annotation { "Feature Type Name" : "Feature", "Feature Type Description" : "" }
export const myFeature = defineFeature(function(context is Context, id is Id, definition is map)
    precondition{}
    {
        {
            var Q0;
            Q0=qCreatedBy(makeId("Top.planeOp"),FACE);
            var sketch = newSketch(context, id + "F0", { "sketchPlane" : qUnion([Q0])});
            skLineSegment(sketch, "E0.bottom", {"start": v(-75.16, -23.95) * mm, "end": v(74.84, -23.95) * mm});
            skLineSegment(sketch, "E0.top", {"start": v(-75.16, -73.95) * mm, "end": v(74.84, -73.95) * mm});
            skLineSegment(sketch, "E0.left", {"start": v(-75.16, -23.95) * mm, "end": v(-75.16, -73.95) * mm});
            skLineSegment(sketch, "E0.right", {"start": v(74.84, -23.95) * mm, "end": v(74.84, -73.95) * mm});
            skSolve(sketch);
        }
        {
            var Q0;
            Q0=makeQuery(id+"F0.imprint","IMPRINT",FACE,{"disambiguationData":[TD([[makeQuery(id+"F0.imprint","IMPRINT",EDGE,{"derivedFrom":sQuery(id+"F0.wireOp",EDGE,"E0.bottom")}),-1.0]])]});
            extrude(context, id + "F1", {"entities" : qUnion([Q0]), "depth" : 100 * mm, "offsetDistance" : 25 * mm});
        }
        {
            var Q0;
            Q0=makeQuery(id+"F1.opExtrude","SWEPT_FACE",FACE,{"disambiguationData":[OSD([sQuery(id+"F0.wireOp",EDGE,"E0.top")])]});
            var sketch = newSketch(context, id + "F2", { "sketchPlane" : qUnion([Q0])});
            skCircle(sketch, "E1", {"center": v(26.87, 49.86) * mm, "radius": 30 * mm});
            skSolve(sketch);
        }
        {
            var Q0;
            Q0=makeQuery(id+"F2.imprint","IMPRINT",FACE,{"disambiguationData":[TD([[makeQuery(id+"F2.imprint","IMPRINT",EDGE,{"derivedFrom":sQuery(id+"F2.wireOp",EDGE,"E1")}),1.0]])]});
            extrude(context, id + "F3", {"entities" : qUnion([Q0]), "operationType" : NewBodyOperationType.ADD, "depth" : 40 * mm, "offsetDistance" : 25 * mm});
        }
        {
            var Q0;
            Q0=makeQuery(id+"F1.opExtrude","CAP_EDGE",EDGE,{"disambiguationData":[OSD([sQuery(id+"F0.wireOp",EDGE,"E0.right")])],"isStart":false});
            var Q1;
            Q1=makeQuery(id+"F1.opExtrude","CAP_EDGE",EDGE,{"disambiguationData":[OSD([sQuery(id+"F0.wireOp",EDGE,"E0.left")])],"isStart":false});
            fillet(context, id + "F4", {"entities" : qUnion([Q0, Q1]), "radius" : 5 * mm, "tangentPropagation" : true, "allowEdgeOverflow" : false});
        }
        {
            var Q0;
            Q0=makeQuery(id+"F3.opExtrude","CAP_EDGE",EDGE,{"disambiguationData":[OSD([sQuery(id+"F2.wireOp",EDGE,"E1")])],"isStart":false});
            chamfer(context, id + "F5", {"entities" : qUnion([Q0]), "width" : 5 * mm, "tangentPropagation" : true});
        }
        {
            var Q0;
            Q0=makeQuery(id+"F1.opExtrude","SWEPT_FACE",FACE,{"disambiguationData":[OSD([sQuery(id+"F0.wireOp",EDGE,"E0.top")])]});
            var sketch = newSketch(context, id + "F6", { "sketchPlane" : qUnion([Q0])});
            skText(sketch, "E2", { "text": "Nikon", "fontName": "RobotoSlab-Bold.ttf"});
            const initialGuessF6  = {"E2": [-0.07516, 0.0048, 1, 0, 0.01836]};
            skSetInitialGuess(sketch, initialGuessF6);
            skSolve(sketch);
        }
        {
            var Q0;
            Q0 = qSketchRegion(id + "F6", true);
            extrude(context, id + "F7", {"entities" : qUnion([Q0]), "operationType" : NewBodyOperationType.REMOVE, "oppositeDirection" : true, "depth" : 2 * mm, "offsetDistance" : 25 * mm});
        }
        {
            var Q0;
            {var subQ0=sQuery(id+"F0.wireOp",EDGE,"E0.left");var subQ2=sQuery(id+"F0.wireOp",EDGE,"E0.top");Q0=makeQuery(id+"F7.boolean.opBoolean","SPLIT",FACE,{"disambiguationData":[TD([makeQuery(id+"F1.opExtrude","SWEPT_FACE",FACE,{"disambiguationData":[OSD([subQ0])]})])],"derivedFrom":makeQuery(id+"F1.opExtrude","SWEPT_FACE",FACE,{"disambiguationData":[OSD([subQ2])]})});}
            var sketch = newSketch(context, id + "F8", { "sketchPlane" : qUnion([Q0])});
            skLineSegment(sketch, "E3.bottom", {"start": v(0, 97.8) * mm, "end": v(25, 97.8) * mm});
            skLineSegment(sketch, "E3.top", {"start": v(0, 87.8) * mm, "end": v(25, 87.8) * mm});
            skLineSegment(sketch, "E3.left", {"start": v(0, 97.8) * mm, "end": v(0, 87.8) * mm});
            skLineSegment(sketch, "E3.right", {"start": v(25, 97.8) * mm, "end": v(25, 87.8) * mm});
            skSolve(sketch);
        }
        {
            var Q0;
            Q0=makeQuery(id+"F8.imprint","IMPRINT",FACE,{"disambiguationData":[TD([[makeQuery(id+"F8.imprint","IMPRINT",EDGE,{"derivedFrom":sQuery(id+"F8.wireOp",EDGE,"E3.bottom")}),-1.0]])]});
            extrude(context, id + "F9", {"entities" : qUnion([Q0]), "operationType" : NewBodyOperationType.REMOVE, "oppositeDirection" : true, "depth" : 5 * mm, "offsetDistance" : 25 * mm});
        }
        {
            var Q0;
            Q0=makeQuery(id+"F1.opExtrude","CAP_FACE",FACE,{"disambiguationData":[OSD([sQuery(id+"F0.wireOp",EDGE,"E0.bottom"),sQuery(id+"F0.wireOp",EDGE,"E0.top"),sQuery(id+"F0.wireOp",EDGE,"E0.left"),sQuery(id+"F0.wireOp",EDGE,"E0.right")])],"isStart":false});
            var sketch = newSketch(context, id + "F10", { "sketchPlane" : qUnion([Q0])});
            skCircle(sketch, "E4", {"center": v(-56.66, -36) * mm, "radius": 7.42 * mm});
            skSolve(sketch);
        }
        {
            var Q0;
            Q0=makeQuery(id+"F10.imprint","IMPRINT",FACE,{"disambiguationData":[TD([[makeQuery(id+"F10.imprint","IMPRINT",EDGE,{"derivedFrom":sQuery(id+"F10.wireOp",EDGE,"E4")}),1.0]])]});
            extrude(context, id + "F11", {"entities" : qUnion([Q0]), "operationType" : NewBodyOperationType.ADD, "depth" : 5 * mm, "offsetDistance" : 25 * mm});
        }
        {
            var Q0;
            Q0=makeQuery(id+"F1.opExtrude","SWEPT_FACE",FACE,{"disambiguationData":[OSD([sQuery(id+"F0.wireOp",EDGE,"E0.bottom")])]});
            var sketch = newSketch(context, id + "F12", { "sketchPlane" : qUnion([Q0])});
            skLineSegment(sketch, "E5.bottom", {"start": v(-69.68, 79.38) * mm, "end": v(19, 79.38) * mm});
            skLineSegment(sketch, "E5.top", {"start": v(-69.68, 14) * mm, "end": v(19, 14) * mm});
            skLineSegment(sketch, "E5.left", {"start": v(-69.68, 79.38) * mm, "end": v(-69.68, 14) * mm});
            skLineSegment(sketch, "E5.right", {"start": v(19, 79.38) * mm, "end": v(19, 14) * mm});
            skSolve(sketch);
        }
        {
            var Q0;
            Q0 = qSketchRegion(id + "F12", true);
            extrude(context, id + "F13", {"entities" : qUnion([Q0]), "operationType" : NewBodyOperationType.ADD, "depth" : 1 * mm, "offsetDistance" : 25 * mm});
        }
        {
            var Q0;
            Q0=makeQuery(id+"F1.opExtrude","SWEPT_FACE",FACE,{"disambiguationData":[OSD([sQuery(id+"F0.wireOp",EDGE,"E0.bottom")])]});
            var sketch = newSketch(context, id + "F14", { "sketchPlane" : qUnion([Q0])});
            skText(sketch, "E6", { "text": "Nikon Revo", "fontName": "RobotoSlab-Bold.ttf"});
            const initialGuessF14  = {"E6": [-0.06856, 0.08341, 1, 0, 0.00806]};
            skSetInitialGuess(sketch, initialGuessF14);
            skSolve(sketch);
        }
        {
            var Q0;
            Q0 = qSketchRegion(id + "F14", true);
            extrude(context, id + "F15", {"entities" : qUnion([Q0]), "operationType" : NewBodyOperationType.REMOVE, "oppositeDirection" : true, "depth" : 2 * mm, "offsetDistance" : 25 * mm});
        }
        {
            var Q0;
            {var subQ0=sQuery(id+"F0.wireOp",EDGE,"E0.left");var subQ3=sQuery(id+"F0.wireOp",EDGE,"E0.bottom");Q0=makeQuery(id+"F15.boolean.opBoolean","SPLIT",FACE,{"disambiguationData":[TD([makeQuery(id+"F1.opExtrude","SWEPT_FACE",FACE,{"disambiguationData":[OSD([subQ0])]})])],"derivedFrom":makeQuery(id+"F1.opExtrude","SWEPT_FACE",FACE,{"disambiguationData":[OSD([subQ3])]})});}
            var sketch = newSketch(context, id + "F16", { "sketchPlane" : qUnion([Q0])});
            skCircle(sketch, "E7", {"center": v(44.98, 61.02) * mm, "radius": 13.57 * mm});
            skSolve(sketch);
        }
        {
            var Q0;
            Q0=makeQuery(id+"F16.imprint","IMPRINT",FACE,{"disambiguationData":[TD([[makeQuery(id+"F16.imprint","IMPRINT",EDGE,{"derivedFrom":sQuery(id+"F16.wireOp",EDGE,"E7")}),-1.0]])]});
            var sketch = newSketch(context, id + "F17", { "sketchPlane" : qUnion([Q0])});
            skSolve(sketch);
        }
        {
            var Q0;
            Q0=makeQuery(id+"F17.imprint","IMPRINT",FACE,{"disambiguationData":[TD([[makeQuery(id+"F17.imprint","IMPRINT",EDGE,{"derivedFrom":makeQuery(id+"F16.imprint","IMPRINT",EDGE,{"derivedFrom":sQuery(id+"F16.wireOp",EDGE,"E7")})}),1.0]])]});
            extrude(context, id + "F18", {"entities" : qUnion([Q0]), "operationType" : NewBodyOperationType.ADD, "depth" : 1.3 * mm, "offsetDistance" : 25 * mm});
        }
        {
            var Q0;
            Q0=makeQuery(id+"F16.imprint","IMPRINT",FACE,{"disambiguationData":[TD([[makeQuery(id+"F16.imprint","IMPRINT",EDGE,{"derivedFrom":sQuery(id+"F16.wireOp",EDGE,"E7")}),-1.0]])]});
            var sketch = newSketch(context, id + "F19", { "sketchPlane" : qUnion([Q0])});
            skCircle(sketch, "E8", {"center": v(44.98, 61.24) * mm, "radius": 5.56 * mm});
            skSolve(sketch);
        }
        {
            var Q0;
            Q0 = qSketchRegion(id + "F19", true);
            extrude(context, id + "F20", {"entities" : qUnion([Q0]), "operationType" : NewBodyOperationType.REMOVE, "oppositeDirection" : true, "depth" : 2.6 * mm, "offsetDistance" : 25 * mm});
        }
        {
            var Q0;
            Q0=makeQuery(id+"F3.opExtrude","CAP_FACE",FACE,{"disambiguationData":[OSD([sQuery(id+"F2.wireOp",EDGE,"E1")])],"isStart":false});
            extrude(context, id + "F21", {"entities" : qUnion([Q0]), "operationType" : NewBodyOperationType.ADD, "depth" : 25 * mm, "offsetDistance" : 25 * mm});
        }
        {
            var Q0;
            Q0=makeQuery(id+"F21.opExtrude","CAP_FACE",FACE,{"disambiguationData":[OSD([sQuery(id+"F2.wireOp",EDGE,"E1")])],"isStart":false});
            extrude(context, id + "F22", {"entities" : qUnion([Q0]), "operationType" : NewBodyOperationType.REMOVE, "oppositeDirection" : true, "depth" : 11.2 * mm, "offsetDistance" : 25 * mm});
        }
        {
            var Q0;
            Q0=makeQuery(id+"F22.boolean.opBoolean","COPY",FACE,{"derivedFrom":makeQuery(id+"F22.opExtrude","CAP_FACE",FACE,{"disambiguationData":[OSD([sQuery(id+"F2.wireOp",EDGE,"E1")])],"isStart":false})});
            extrude(context, id + "F23", {"entities" : qUnion([Q0]), "operationType" : NewBodyOperationType.ADD, "depth" : 6.1 * mm, "offsetDistance" : 25 * mm});
        }
        {
            var Q0;
            Q0=makeQuery(id+"F23.opExtrude","CAP_FACE",FACE,{"disambiguationData":[OSD([sQuery(id+"F2.wireOp",EDGE,"E1")])],"isStart":false});
            var sketch = newSketch(context, id + "F24", { "sketchPlane" : qUnion([Q0])});
            skCircle(sketch, "E9", {"center": v(26.87, 49.86) * mm, "radius": 21.07 * mm});
            skSolve(sketch);
        }
        {
            var Q0;
            Q0 = qSketchRegion(id + "F24", true);
            extrude(context, id + "F25", {"entities" : qUnion([Q0]), "operationType" : NewBodyOperationType.REMOVE, "oppositeDirection" : true, "depth" : 23.1 * mm, "offsetDistance" : 25 * mm});
        }
        {
            var Q0;
            Q0=makeQuery(id+"F13.opExtrude","CAP_FACE",FACE,{"disambiguationData":[OSD([sQuery(id+"F12.wireOp",EDGE,"E5.bottom"),sQuery(id+"F12.wireOp",EDGE,"E5.top"),sQuery(id+"F12.wireOp",EDGE,"E5.left"),sQuery(id+"F12.wireOp",EDGE,"E5.right")])],"isStart":false});
            extrude(context, id + "F26", {"entities" : qUnion([Q0]), "depth" : 1.1 * mm, "offsetDistance" : 25 * mm});
        }
        {
            var Q0;
            Q0=makeQuery(id+"F18.opExtrude","CAP_FACE",FACE,{"disambiguationData":[OSD([sQuery(id+"F16.wireOp",EDGE,"E7")])],"isStart":false});
            extrude(context, id + "F27", {"entities" : qUnion([Q0]), "depth" : 0.5 * mm, "offsetDistance" : 25 * mm});
        }
        {
            var Q0;
            Q0=makeQuery(id+"F25.boolean.opBoolean","COPY",FACE,{"derivedFrom":makeQuery(id+"F25.opExtrude","CAP_FACE",FACE,{"disambiguationData":[OSD([sQuery(id+"F24.wireOp",EDGE,"E9")])],"isStart":false})});
            extrude(context, id + "F28", {"entities" : qUnion([Q0]), "depth" : 0.1 * mm, "offsetDistance" : 25 * mm});
        }
        {
            var Q0;
            Q0=makeQuery(id+"F28.opExtrude","CAP_FACE",FACE,{"disambiguationData":[OSD([sQuery(id+"F24.wireOp",EDGE,"E9")])],"isStart":false});
            extrude(context, id + "F29", {"entities" : qUnion([Q0]), "oppositeDirection" : true, "depth" : 1.5 * mm, "offsetDistance" : 25 * mm});
        }
        {
            var Q0;
            Q0=makeQuery(id+"F28.opExtrude","CAP_FACE",FACE,{"disambiguationData":[OSD([sQuery(id+"F24.wireOp",EDGE,"E9")])],"isStart":false});
            extrude(context, id + "F30", {"entities" : qUnion([Q0]), "oppositeDirection" : true, "depth" : 7.1 * mm, "offsetDistance" : 25 * mm});
        }
        {
            var Q0;
            {var subQ0=sQuery(id+"F0.wireOp",EDGE,"E0.left");var subQ2=sQuery(id+"F0.wireOp",EDGE,"E0.top");Q0=makeQuery(id+"F7.boolean.opBoolean","SPLIT",FACE,{"disambiguationData":[TD([makeQuery(id+"F1.opExtrude","SWEPT_FACE",FACE,{"disambiguationData":[OSD([subQ0])]})])],"derivedFrom":makeQuery(id+"F1.opExtrude","SWEPT_FACE",FACE,{"disambiguationData":[OSD([subQ2])]})});}
            var sketch = newSketch(context, id + "F31", { "sketchPlane" : qUnion([Q0])});
            skCircle(sketch, "E10", {"center": v(63.63, 93.94) * mm, "radius": 4.48 * mm});
            skSolve(sketch);
        }
        {
            var Q0;
            Q0 = qSketchRegion(id + "F31", true);
            extrude(context, id + "F32", {"entities" : qUnion([Q0]), "oppositeDirection" : true, "depth" : 1.7 * mm, "offsetDistance" : 25 * mm});
        }
        {
            var Q0;
            Q0=makeQuery(id+"F28.opExtrude","CAP_FACE",FACE,{"disambiguationData":[OSD([sQuery(id+"F24.wireOp",EDGE,"E9")])],"isStart":false});
            extrude(context, id + "F33", {"entities" : qUnion([Q0]), "oppositeDirection" : true, "depth" : 7.3 * mm, "offsetDistance" : 25 * mm});
        }
        {
            var Q0;
            Q0=makeQuery(id+"F7.boolean.opBoolean","COPY",FACE,{"derivedFrom":makeQuery(id+"F7.opExtrude","CAP_FACE",FACE,{"disambiguationData":[OSD([sQuery(id+"F6.wireOp",EDGE,"E2.sketch_text.stroke-38"),sQuery(id+"F6.wireOp",EDGE,"E2.sketch_text.stroke-39"),sQuery(id+"F6.wireOp",EDGE,"E2.sketch_text.stroke-40"),sQuery(id+"F6.wireOp",EDGE,"E2.sketch_text.stroke-41"),sQuery(id+"F6.wireOp",EDGE,"E2.sketch_text.stroke-42"),sQuery(id+"F6.wireOp",EDGE,"E2.sketch_text.stroke-43"),sQuery(id+"F6.wireOp",EDGE,"E2.sketch_text.stroke-44"),sQuery(id+"F6.wireOp",EDGE,"E2.sketch_text.stroke-45"),sQuery(id+"F6.wireOp",EDGE,"E2.sketch_text.stroke-46"),sQuery(id+"F6.wireOp",EDGE,"E2.sketch_text.stroke-47"),sQuery(id+"F6.wireOp",EDGE,"E2.sketch_text.stroke-48"),sQuery(id+"F6.wireOp",EDGE,"E2.sketch_text.stroke-49"),sQuery(id+"F6.wireOp",EDGE,"E2.sketch_text.stroke-50"),sQuery(id+"F6.wireOp",EDGE,"E2.sketch_text.stroke-51"),sQuery(id+"F6.wireOp",EDGE,"E2.sketch_text.stroke-52"),sQuery(id+"F6.wireOp",EDGE,"E2.sketch_text.stroke-53"),sQuery(id+"F6.wireOp",EDGE,"E2.sketch_text.stroke-54"),sQuery(id+"F6.wireOp",EDGE,"E2.sketch_text.stroke-55"),sQuery(id+"F6.wireOp",EDGE,"E2.sketch_text.stroke-56"),sQuery(id+"F6.wireOp",EDGE,"E2.sketch_text.stroke-57"),sQuery(id+"F6.wireOp",EDGE,"E2.sketch_text.stroke-58"),sQuery(id+"F6.wireOp",EDGE,"E2.sketch_text.stroke-59"),sQuery(id+"F6.wireOp",EDGE,"E2.sketch_text.stroke-60"),sQuery(id+"F6.wireOp",EDGE,"E2.sketch_text.stroke-61"),sQuery(id+"F6.wireOp",EDGE,"E2.sketch_text.stroke-62"),sQuery(id+"F6.wireOp",EDGE,"E2.sketch_text.stroke-63"),sQuery(id+"F6.wireOp",EDGE,"E2.sketch_text.stroke-64")])],"isStart":false})});
            var Q1;
            Q1=makeQuery(id+"F7.boolean.opBoolean","COPY",FACE,{"derivedFrom":makeQuery(id+"F7.opExtrude","CAP_FACE",FACE,{"disambiguationData":[OSD([sQuery(id+"F6.wireOp",EDGE,"E2.sketch_text.stroke-24"),sQuery(id+"F6.wireOp",EDGE,"E2.sketch_text.stroke-25"),sQuery(id+"F6.wireOp",EDGE,"E2.sketch_text.stroke-26"),sQuery(id+"F6.wireOp",EDGE,"E2.sketch_text.stroke-27"),sQuery(id+"F6.wireOp",EDGE,"E2.sketch_text.stroke-28"),sQuery(id+"F6.wireOp",EDGE,"E2.sketch_text.stroke-29"),sQuery(id+"F6.wireOp",EDGE,"E2.sketch_text.stroke-30"),sQuery(id+"F6.wireOp",EDGE,"E2.sketch_text.stroke-31"),sQuery(id+"F6.wireOp",EDGE,"E2.sketch_text.stroke-32"),sQuery(id+"F6.wireOp",EDGE,"E2.sketch_text.stroke-33")])],"isStart":false})});
            var Q2;
            Q2=makeQuery(id+"F7.boolean.opBoolean","COPY",FACE,{"derivedFrom":makeQuery(id+"F7.opExtrude","CAP_FACE",FACE,{"disambiguationData":[OSD([sQuery(id+"F6.wireOp",EDGE,"E2.sketch_text.stroke-0"),sQuery(id+"F6.wireOp",EDGE,"E2.sketch_text.stroke-1"),sQuery(id+"F6.wireOp",EDGE,"E2.sketch_text.stroke-2"),sQuery(id+"F6.wireOp",EDGE,"E2.sketch_text.stroke-3"),sQuery(id+"F6.wireOp",EDGE,"E2.sketch_text.stroke-4"),sQuery(id+"F6.wireOp",EDGE,"E2.sketch_text.stroke-5"),sQuery(id+"F6.wireOp",EDGE,"E2.sketch_text.stroke-6"),sQuery(id+"F6.wireOp",EDGE,"E2.sketch_text.stroke-7"),sQuery(id+"F6.wireOp",EDGE,"E2.sketch_text.stroke-8"),sQuery(id+"F6.wireOp",EDGE,"E2.sketch_text.stroke-9"),sQuery(id+"F6.wireOp",EDGE,"E2.sketch_text.stroke-10"),sQuery(id+"F6.wireOp",EDGE,"E2.sketch_text.stroke-11"),sQuery(id+"F6.wireOp",EDGE,"E2.sketch_text.stroke-12"),sQuery(id+"F6.wireOp",EDGE,"E2.sketch_text.stroke-13"),sQuery(id+"F6.wireOp",EDGE,"E2.sketch_text.stroke-14"),sQuery(id+"F6.wireOp",EDGE,"E2.sketch_text.stroke-15"),sQuery(id+"F6.wireOp",EDGE,"E2.sketch_text.stroke-16"),sQuery(id+"F6.wireOp",EDGE,"E2.sketch_text.stroke-17"),sQuery(id+"F6.wireOp",EDGE,"E2.sketch_text.stroke-18"),sQuery(id+"F6.wireOp",EDGE,"E2.sketch_text.stroke-19"),sQuery(id+"F6.wireOp",EDGE,"E2.sketch_text.stroke-20"),sQuery(id+"F6.wireOp",EDGE,"E2.sketch_text.stroke-21"),sQuery(id+"F6.wireOp",EDGE,"E2.sketch_text.stroke-22"),sQuery(id+"F6.wireOp",EDGE,"E2.sketch_text.stroke-23")])],"isStart":false})});
            var Q3;
            Q3=makeQuery(id+"F7.boolean.opBoolean","COPY",FACE,{"derivedFrom":makeQuery(id+"F7.opExtrude","CAP_FACE",FACE,{"disambiguationData":[OSD([sQuery(id+"F6.wireOp",EDGE,"E2.sketch_text.stroke-65"),sQuery(id+"F6.wireOp",EDGE,"E2.sketch_text.stroke-66"),sQuery(id+"F6.wireOp",EDGE,"E2.sketch_text.stroke-67"),sQuery(id+"F6.wireOp",EDGE,"E2.sketch_text.stroke-68"),sQuery(id+"F6.wireOp",EDGE,"E2.sketch_text.stroke-69"),sQuery(id+"F6.wireOp",EDGE,"E2.sketch_text.stroke-70"),sQuery(id+"F6.wireOp",EDGE,"E2.sketch_text.stroke-71"),sQuery(id+"F6.wireOp",EDGE,"E2.sketch_text.stroke-72"),sQuery(id+"F6.wireOp",EDGE,"E2.sketch_text.stroke-73"),sQuery(id+"F6.wireOp",EDGE,"E2.sketch_text.stroke-74"),sQuery(id+"F6.wireOp",EDGE,"E2.sketch_text.stroke-75"),sQuery(id+"F6.wireOp",EDGE,"E2.sketch_text.stroke-76"),sQuery(id+"F6.wireOp",EDGE,"E2.sketch_text.stroke-77"),sQuery(id+"F6.wireOp",EDGE,"E2.sketch_text.stroke-78"),sQuery(id+"F6.wireOp",EDGE,"E2.sketch_text.stroke-79"),sQuery(id+"F6.wireOp",EDGE,"E2.sketch_text.stroke-80"),sQuery(id+"F6.wireOp",EDGE,"E2.sketch_text.stroke-81"),sQuery(id+"F6.wireOp",EDGE,"E2.sketch_text.stroke-82"),sQuery(id+"F6.wireOp",EDGE,"E2.sketch_text.stroke-83"),sQuery(id+"F6.wireOp",EDGE,"E2.sketch_text.stroke-84")])],"isStart":false})});
            var Q4;
            Q4=makeQuery(id+"F7.boolean.opBoolean","COPY",FACE,{"derivedFrom":makeQuery(id+"F7.opExtrude","CAP_FACE",FACE,{"disambiguationData":[OSD([sQuery(id+"F6.wireOp",EDGE,"E2.sketch_text.stroke-85"),sQuery(id+"F6.wireOp",EDGE,"E2.sketch_text.stroke-86"),sQuery(id+"F6.wireOp",EDGE,"E2.sketch_text.stroke-87"),sQuery(id+"F6.wireOp",EDGE,"E2.sketch_text.stroke-88"),sQuery(id+"F6.wireOp",EDGE,"E2.sketch_text.stroke-89"),sQuery(id+"F6.wireOp",EDGE,"E2.sketch_text.stroke-90"),sQuery(id+"F6.wireOp",EDGE,"E2.sketch_text.stroke-91"),sQuery(id+"F6.wireOp",EDGE,"E2.sketch_text.stroke-92"),sQuery(id+"F6.wireOp",EDGE,"E2.sketch_text.stroke-93"),sQuery(id+"F6.wireOp",EDGE,"E2.sketch_text.stroke-94"),sQuery(id+"F6.wireOp",EDGE,"E2.sketch_text.stroke-95"),sQuery(id+"F6.wireOp",EDGE,"E2.sketch_text.stroke-96"),sQuery(id+"F6.wireOp",EDGE,"E2.sketch_text.stroke-97"),sQuery(id+"F6.wireOp",EDGE,"E2.sketch_text.stroke-98"),sQuery(id+"F6.wireOp",EDGE,"E2.sketch_text.stroke-99"),sQuery(id+"F6.wireOp",EDGE,"E2.sketch_text.stroke-100"),sQuery(id+"F6.wireOp",EDGE,"E2.sketch_text.stroke-101"),sQuery(id+"F6.wireOp",EDGE,"E2.sketch_text.stroke-102"),sQuery(id+"F6.wireOp",EDGE,"E2.sketch_text.stroke-103"),sQuery(id+"F6.wireOp",EDGE,"E2.sketch_text.stroke-104"),sQuery(id+"F6.wireOp",EDGE,"E2.sketch_text.stroke-105"),sQuery(id+"F6.wireOp",EDGE,"E2.sketch_text.stroke-106"),sQuery(id+"F6.wireOp",EDGE,"E2.sketch_text.stroke-107"),sQuery(id+"F6.wireOp",EDGE,"E2.sketch_text.stroke-108"),sQuery(id+"F6.wireOp",EDGE,"E2.sketch_text.stroke-109"),sQuery(id+"F6.wireOp",EDGE,"E2.sketch_text.stroke-110")])],"isStart":false})});
            extrude(context, id + "F34", {"entities" : qUnion([Q0, Q1, Q2, Q3, Q4]), "oppositeDirection" : true, "depth" : 1.5 * mm, "offsetDistance" : 25 * mm});
        }
    });